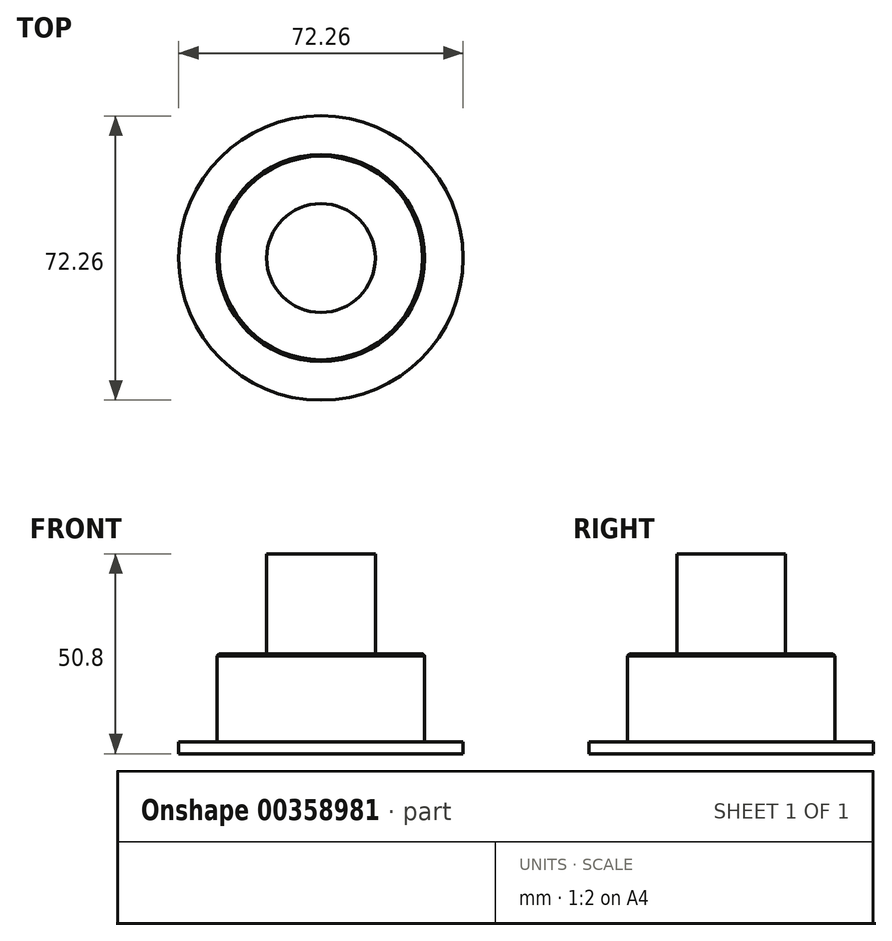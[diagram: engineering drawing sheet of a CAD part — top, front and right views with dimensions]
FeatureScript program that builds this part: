
annotation { "Feature Type Name" : "Feature", "Feature Type Description" : "" }
export const myFeature = defineFeature(function(context is Context, id is Id, definition is map)
    precondition{}
    {
        {
            var Q0;
            Q0=qCreatedBy(makeId("Top.planeOp"),FACE);
            var sketch = newSketch(context, id + "F0", { "sketchPlane" : qUnion([Q0])});
            skCircle(sketch, "E0", {"center": v(0, 0) * mm, "radius": 36.13 * mm});
            skSolve(sketch);
        }
        {
            var Q0;
            Q0=makeQuery(id+"F0.imprint","IMPRINT",FACE,{"disambiguationData":[TD([[makeQuery(id+"F0.imprint","IMPRINT",EDGE,{"derivedFrom":sQuery(id+"F0.wireOp",EDGE,"E0")}),1.0]])]});
            var Q1;
            Q1=sQuery(id+"F0.wireOp",EDGE,"E0");
            extrude(context, id + "F1", {"entities" : qUnion([Q0]), "surfaceEntities" : qUnion([Q1]), "depth" : 3 * mm});
        }
        {
            var Q0;
            Q0=qCreatedBy(makeId("Top.planeOp"),FACE);
            var sketch = newSketch(context, id + "F2", { "sketchPlane" : qUnion([Q0])});
            skCircle(sketch, "E1", {"center": v(0, 0) * mm, "radius": 26.35 * mm});
            skSolve(sketch);
        }
        {
            var Q0;
            Q0 = qSketchRegion(id + "F2", true);
            extrude(context, id + "F3", {"entities" : qUnion([Q0]), "operationType" : NewBodyOperationType.ADD, "depth" : 25.4 * mm});
        }
        {
            var Q0;
            Q0=makeQuery(id+"F3.opExtrude","CAP_FACE",FACE,{"disambiguationData":[OSD([sQuery(id+"F2.wireOp",EDGE,"E1")])],"isStart":false});
            var sketch = newSketch(context, id + "F4", { "sketchPlane" : qUnion([Q0])});
            skCircle(sketch, "E2", {"center": v(0, 0) * mm, "radius": 13.8 * mm});
            skSolve(sketch);
        }
        {
            var Q0;
            Q0 = qSketchRegion(id + "F4", true);
            extrude(context, id + "F5", {"entities" : qUnion([Q0]), "operationType" : NewBodyOperationType.ADD, "depth" : 25.4 * mm});
        }
        {
            var Q0;
            Q0=makeQuery(id+"F3.opExtrude","CAP_EDGE",EDGE,{"disambiguationData":[OSD([sQuery(id+"F2.wireOp",EDGE,"E1")])],"isStart":false});
            chamfer(context, id + "F6", {"entities" : qUnion([Q0]), "width" : 0.5 * mm, "tangentPropagation" : true});
        }
    });
